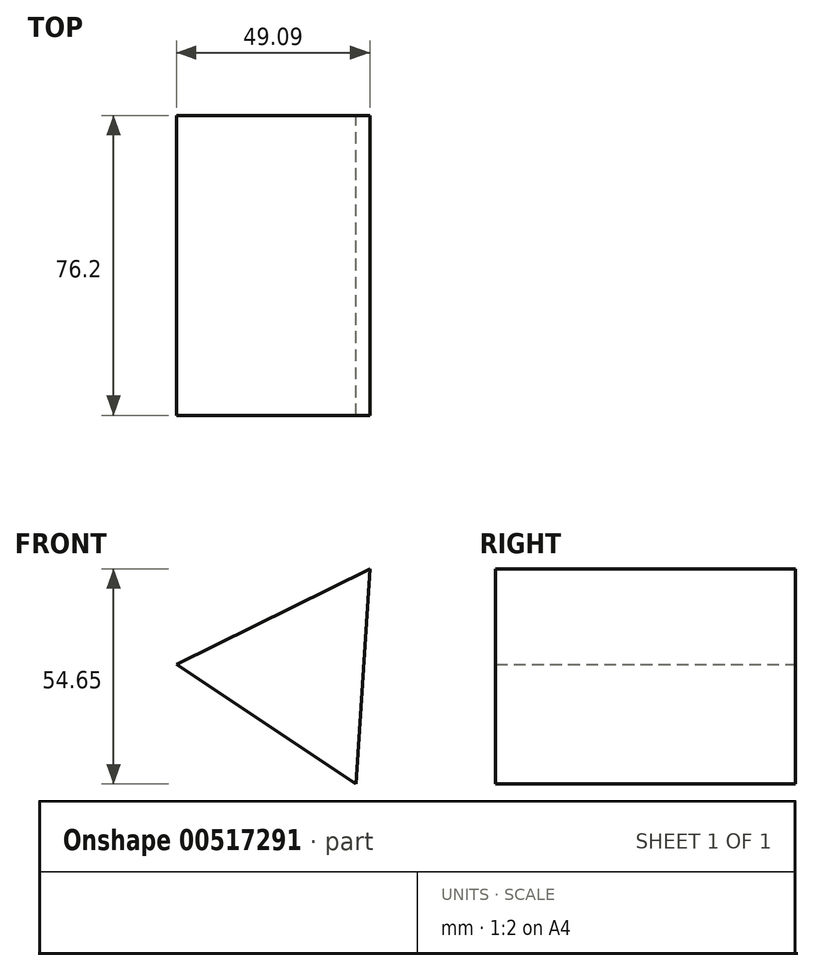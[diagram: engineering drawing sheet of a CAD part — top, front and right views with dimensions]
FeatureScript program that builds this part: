
annotation { "Feature Type Name" : "Feature", "Feature Type Description" : "" }
export const myFeature = defineFeature(function(context is Context, id is Id, definition is map)
    precondition{}
    {
        {
            var Q0;
            Q0=qCreatedBy(makeId("Front.planeOp"),FACE);
            var sketch = newSketch(context, id + "F0", { "sketchPlane" : qUnion([Q0])});
            skLineSegment(sketch, "E0.0", {"start": v(-37.5, 1.17) * mm, "end": v(11.6, 25.45) * mm});
            skLineSegment(sketch, "E0.1", {"start": v(11.6, 25.45) * mm, "end": v(8.07, -29.2) * mm});
            skLineSegment(sketch, "E0.2", {"start": v(8.07, -29.2) * mm, "end": v(-37.5, 1.17) * mm});
            skPoint(sketch, "E0.0.midPoint", {"position": v(-12.95, 13.3) * mm});
            skSolve(sketch);
        }
        {
            var Q0;
            Q0 = qSketchRegion(id + "F0", true);
            extrude(context, id + "F1", {"entities" : qUnion([Q0]), "depth" : 76.2 * mm, "offsetDistance" : 25.4 * mm});
        }
    });
